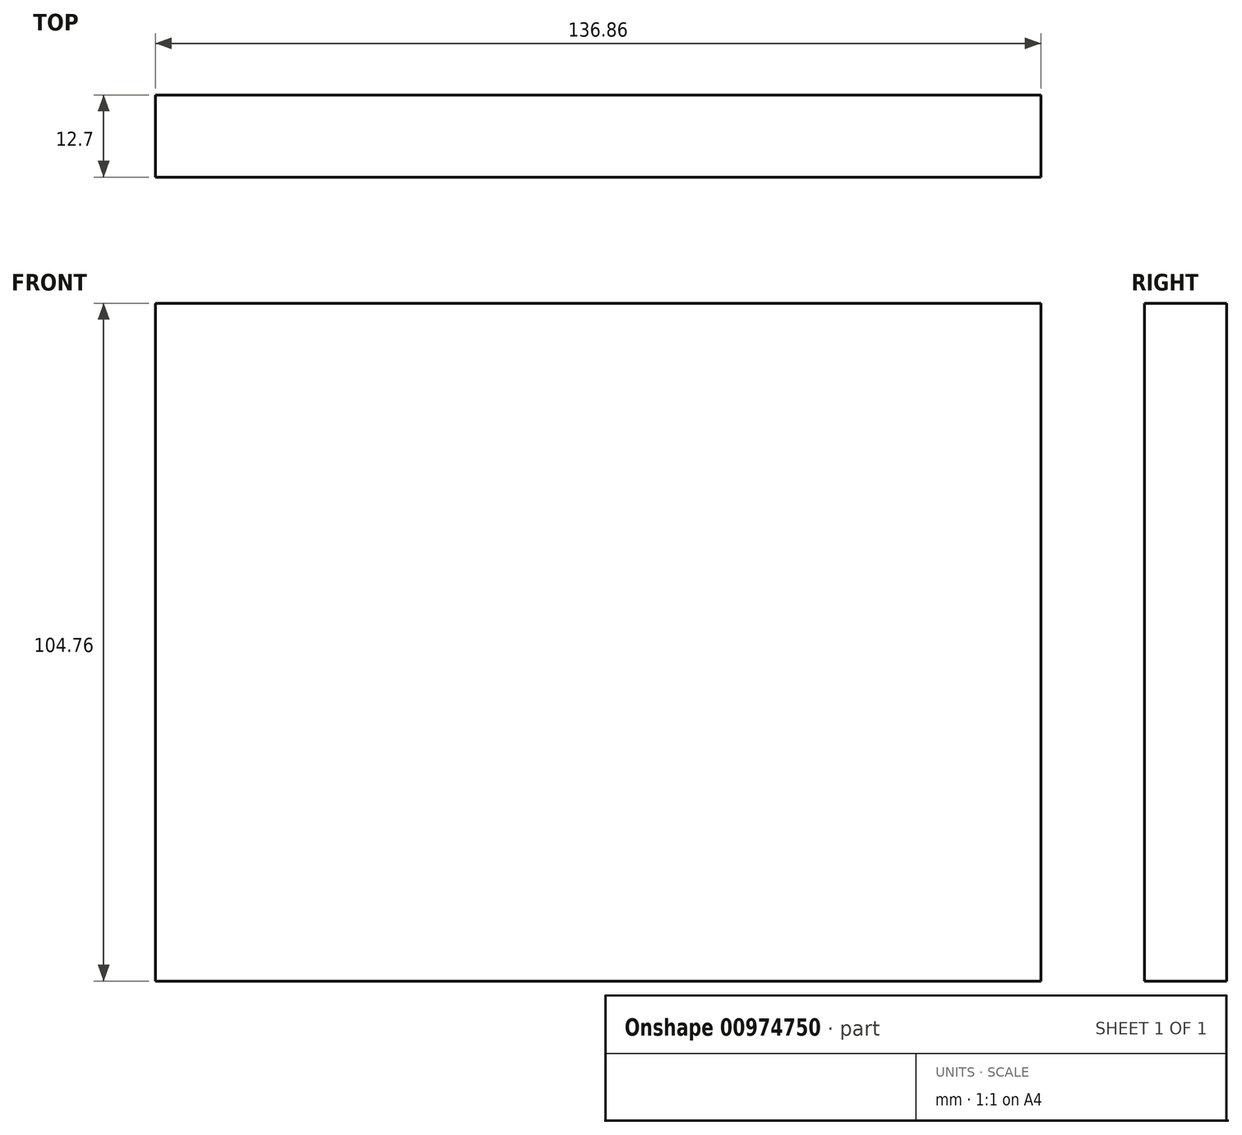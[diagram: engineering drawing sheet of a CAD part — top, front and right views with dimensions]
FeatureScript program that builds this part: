
annotation { "Feature Type Name" : "Feature", "Feature Type Description" : "" }
export const myFeature = defineFeature(function(context is Context, id is Id, definition is map)
    precondition{}
    {
        {
            var Q0;
            Q0=qCreatedBy(makeId("Front.planeOp"),FACE);
            var sketch = newSketch(context, id + "F0", { "sketchPlane" : qUnion([Q0])});
            skLineSegment(sketch, "E0.bottom", {"start": v(68.43, -52.38) * mm, "end": v(-68.43, -52.38) * mm});
            skLineSegment(sketch, "E0.top", {"start": v(68.43, 52.38) * mm, "end": v(-68.43, 52.38) * mm});
            skLineSegment(sketch, "E0.left", {"start": v(68.43, -52.38) * mm, "end": v(68.43, 52.38) * mm});
            skLineSegment(sketch, "E0.right", {"start": v(-68.43, -52.38) * mm, "end": v(-68.43, 52.38) * mm});
            skPoint(sketch, "E0.middle", {"position": v(0, 0) * mm});
            skSolve(sketch);
        }
        {
            var Q0;
            Q0=makeQuery(id+"F0.imprint","IMPRINT",FACE,{"disambiguationData":[TD([[makeQuery(id+"F0.imprint","IMPRINT",EDGE,{"derivedFrom":sQuery(id+"F0.wireOp",EDGE,"E0.bottom")}),-1.0]])]});
            extrude(context, id + "F1", {"entities" : qUnion([Q0]), "depth" : 12.7 * mm, "offsetDistance" : 25.4 * mm});
        }
    });
